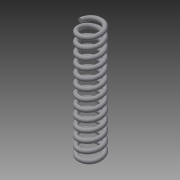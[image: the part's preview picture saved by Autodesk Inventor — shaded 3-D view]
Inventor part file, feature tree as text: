
AUTODESK INVENTOR PART (.ipt)
format: ipt  version: 2014 SP1 (Build 180222100, 222)  size: 439,808 bytes
history: native  units: in
note: dims shown in document units (in); Inventor stores cm internally (conversion verified against a paired STEP export)
features: helix x1, sketch x1
ambient origin geometry x8: Origin, YZ Plane, XZ Plane, XY Plane, X Axis, Y Axis, Z Axis, Center Point
bodies: Solid1 (feature_tree)
feature tree (2):
  helix  "Coil1"  [1 undecoded]
  sketch  "Sketch1"  dims[d1=0.0185in d2=0.5in d3=0.4815in d4=1.0in d5=0.4815in d6=4.7244in d7=0.0in d8=90.0deg d9=90.0deg d10=90.0deg d11=90.0deg]
note: 1 required parameter value undecoded (feature->parameter linkage not recoverable at this tier; creation-order binding heuristic only, values carry confidence <= 0.55)
